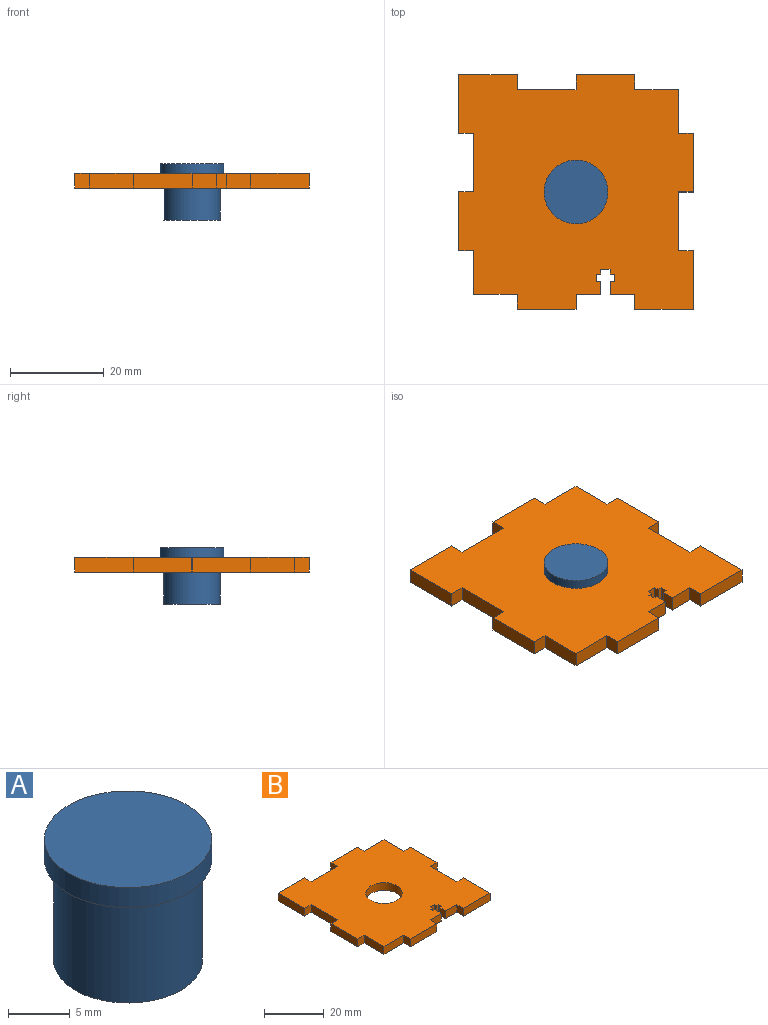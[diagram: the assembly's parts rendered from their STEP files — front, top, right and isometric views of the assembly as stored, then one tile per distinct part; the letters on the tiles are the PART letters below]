
ASSEMBLY  parts=2 mates=1
PART A: 5 faces, bbox 13.6x13.6x12 mm
  f0: cylinder r=6.05mm len=12.1mm, axis (0,0,-1), area 380.1mm2, adj f1,f3
  f1: plane 12.1x12.1mm, normal (0,0,-1), area 115mm2, adj f0
  f2: cylinder r=6.8mm len=13.6mm, axis (0,0,-1), area 85.5mm2, adj f3,f4
  f3: plane 13.6x13.6mm, normal (0,0,-1), area 30.3mm2, adj f0,f2
  f4: plane 13.6x13.6mm, normal (0,0,1), area 145.3mm2, adj f2
PART B: 43 faces, bbox 50x50x3.2 mm
  f0: plane 5.25x3.18mm, normal (0,-1,0), area 16.7mm2, adj f1,f11,f30,f33
  f1: plane 50x50mm, normal (0,0,-1), area 2074.3mm2, adj f0,f2,f3,f4,f5,f6,f7,f8
  f2: plane 3.18x3.18mm, normal (0,-1,0), area 10.1mm2, adj f1,f3,f29,f30
  f3: plane 12.5x3.18mm, normal (-1,0,0), area 39.7mm2, adj f1,f2,f4,f30
  f4: plane 3.18x3.18mm, normal (0,1,0), area 10.1mm2, adj f1,f3,f5,f30
  f5: plane 12.5x3.18mm, normal (-1,0,0), area 39.7mm2, adj f1,f4,f6,f30
  f6: plane 3.18x3.18mm, normal (0,-1,0), area 10.1mm2, adj f1,f5,f7,f30
  f7: plane 9.33x3.18mm, normal (-1,0,0), area 29.6mm2, adj f1,f6,f8,f30
  f8: plane 9.33x3.18mm, normal (0,-1,0), area 29.6mm2, adj f1,f7,f9,f30
  f9: plane 3.18x3.18mm, normal (-1,0,0), area 10.1mm2, adj f1,f8,f10,f30
  f10: plane 12.5x3.18mm, normal (0,-1,0), area 39.7mm2, adj f1,f9,f11,f30
  f11: plane 3.18x3.18mm, normal (1,0,0), area 10.1mm2, adj f0,f1,f10,f30
  f12: plane 5.25x3.18mm, normal (0,-1,0), area 16.7mm2, adj f1,f13,f30,f34
  f13: plane 3.18x3.18mm, normal (-1,0,0), area 10.1mm2, adj f1,f12,f14,f30
  f14: plane 12.5x3.18mm, normal (0,-1,0), area 39.7mm2, adj f1,f13,f15,f30
  f15: plane 12.5x3.18mm, normal (1,0,0), area 39.7mm2, adj f1,f14,f16,f30
  f16: plane 3.18x3.18mm, normal (0,1,0), area 10.1mm2, adj f1,f15,f17,f30
  f17: plane 12.5x3.18mm, normal (1,0,0), area 39.7mm2, adj f1,f16,f18,f30
  f18: plane 3.18x3.18mm, normal (0,-1,0), area 10.1mm2, adj f1,f17,f19,f30
  f19: plane 12.5x3.18mm, normal (1,0,0), area 39.7mm2, adj f1,f18,f20,f30
  f20: plane 3.18x3.18mm, normal (0,1,0), area 10.1mm2, adj f1,f19,f21,f30
  f21: plane 9.33x3.18mm, normal (1,0,0), area 29.6mm2, adj f1,f20,f22,f30
  f22: plane 9.33x3.18mm, normal (0,1,0), area 29.6mm2, adj f1,f21,f23,f30
  f23: plane 3.18x3.18mm, normal (1,0,0), area 10.1mm2, adj f1,f22,f24,f30
  f24: plane 12.5x3.18mm, normal (0,1,0), area 39.7mm2, adj f1,f23,f25,f30
  f25: plane 3.18x3.18mm, normal (-1,0,0), area 10.1mm2, adj f1,f24,f26,f30
  f26: plane 12.5x3.18mm, normal (0,1,0), area 39.7mm2, adj f1,f25,f27,f30
  f27: plane 3.18x3.18mm, normal (1,0,0), area 10.1mm2, adj f1,f26,f28,f30
  f28: plane 12.5x3.18mm, normal (0,1,0), area 39.7mm2, adj f1,f27,f29,f30
  f29: plane 12.5x3.18mm, normal (-1,0,0), area 39.7mm2, adj f1,f2,f28,f30
  f30: plane 50x50mm, normal (0,0,1), area 2074.3mm2, adj f0,f2,f3,f4,f5,f6,f7,f8
  f31: cylinder r=6.05mm len=12.1mm, axis (0,0,-1), area 120.7mm2, adj f1,f30
  f32: plane 3.18x0.9mm, normal (0,1,0), area 2.9mm2, adj f1,f30,f33,f42
  f33: plane 3.18x2.83mm, normal (1,0,0), area 9mm2, adj f0,f1,f30,f32
  f34: plane 3.18x2.83mm, normal (-1,0,0), area 9mm2, adj f1,f12,f30,f35
  f35: plane 3.18x0.9mm, normal (0,1,0), area 2.9mm2, adj f1,f30,f34,f36
  f36: plane 3.18x1.5mm, normal (-1,0,0), area 4.8mm2, adj f1,f30,f35,f37
  f37: plane 3.18x0.9mm, normal (0,-1,0), area 2.9mm2, adj f1,f30,f36,f38
  f38: plane 3.18x1mm, normal (-1,0,0), area 3.2mm2, adj f1,f30,f37,f39
  f39: plane 3.18x2mm, normal (0,-1,0), area 6.3mm2, adj f1,f30,f38,f40
  f40: plane 3.18x1mm, normal (1,0,0), area 3.2mm2, adj f1,f30,f39,f41
  f41: plane 3.18x0.9mm, normal (0,-1,0), area 2.9mm2, adj f1,f30,f40,f42
  f42: plane 3.18x1.5mm, normal (1,0,0), area 4.8mm2, adj f1,f30,f32,f41
PLACE A t=(-6.19,-1.12,-16.34)mm
PLACE B t=(-6.19,-1.12,-9.52)mm
MATE fastened A.f2 <-> B.f31  axis (0,0,-1) through (-6.19,-1.12,-6.34)mm
